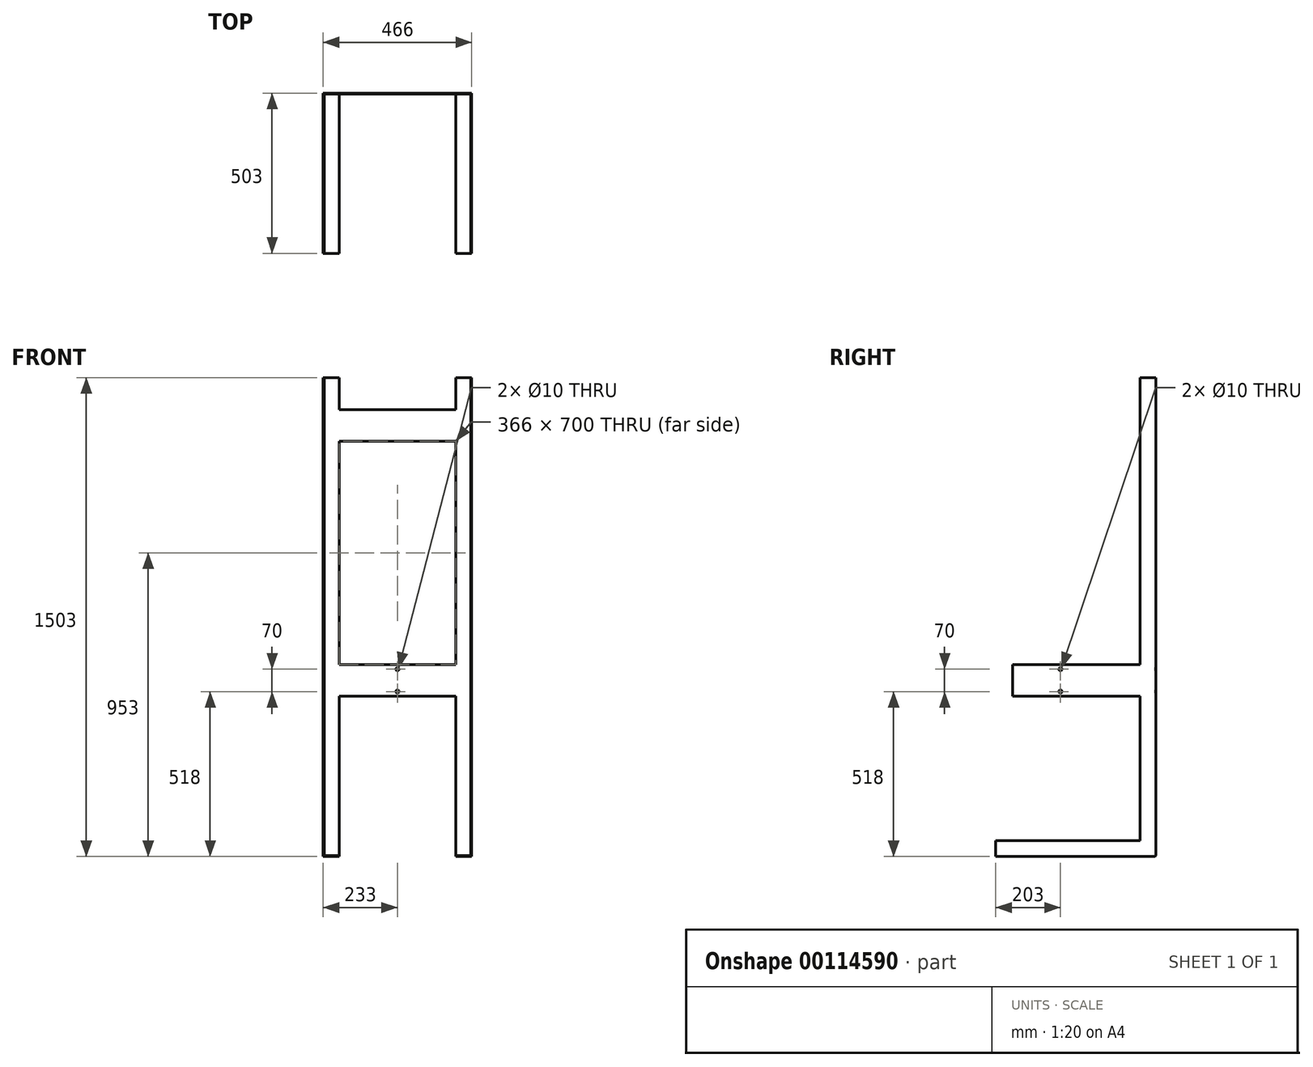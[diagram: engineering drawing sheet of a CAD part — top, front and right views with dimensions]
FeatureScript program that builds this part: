
annotation { "Feature Type Name" : "Feature", "Feature Type Description" : "" }
export const myFeature = defineFeature(function(context is Context, id is Id, definition is map)
    precondition{}
    {
        {
            var Q0;
            Q0=qCreatedBy(makeId("Top.planeOp"),FACE);
            var sketch = newSketch(context, id + "F0", { "sketchPlane" : qUnion([Q0])});
            skLineSegment(sketch, "E0", {"start": v(-233, 225) * mm, "end": v(-233, 175) * mm});
            skLineSegment(sketch, "E1", {"start": v(-233, 175) * mm, "end": v(-230, 175) * mm});
            skLineSegment(sketch, "E2", {"start": v(-230, 175) * mm, "end": v(-230, 222) * mm});
            skLineSegment(sketch, "E3", {"start": v(-183, 222) * mm, "end": v(-230, 222) * mm});
            skLineSegment(sketch, "E4", {"start": v(-233, 225) * mm, "end": v(-183, 225) * mm});
            skLineSegment(sketch, "E5", {"start": v(-183, 222) * mm, "end": v(-183, 225) * mm});
            skSolve(sketch);
        }
        {
            var Q0;
            Q0=makeQuery(id+"F0.imprint","IMPRINT",FACE,{"disambiguationData":[TD([[makeQuery(id+"F0.imprint","IMPRINT",EDGE,{"derivedFrom":sQuery(id+"F0.wireOp",EDGE,"E0")}),1.0]])]});
            extrude(context, id + "F1", {"entities" : qUnion([Q0]), "depth" : 1500 * mm});
        }
        {
            var Q0;
            Q0=makeQuery(id+"F1.opExtrude","SWEPT_FACE",FACE,{"disambiguationData":[OSD([sQuery(id+"F0.wireOp",EDGE,"E5")])]});
            var sketch = newSketch(context, id + "F2", { "sketchPlane" : qUnion([Q0])});
            skLineSegment(sketch, "E6", {"start": v(222, 0) * mm, "end": v(222, -3) * mm});
            skLineSegment(sketch, "E7", {"start": v(222, -3) * mm, "end": v(225, 0) * mm});
            skSolve(sketch);
        }
        {
            var Q0;
            {var subQ0=sQuery(id+"F2.wireOp",EDGE,"E6");Q0=makeQuery(id+"F2.imprint","IMPRINT",FACE,{"disambiguationData":[TD([[makeQuery(id+"F2.imprint","IMPRINT",EDGE,{"derivedFrom":subQ0}),1.0]])]});}
            extrude(context, id + "F3", {"entities" : qUnion([Q0]), "operationType" : NewBodyOperationType.ADD, "oppositeDirection" : true, "depth" : 50 * mm});
        }
        {
            var Q0;
            Q0=makeQuery(id+"F3.boolean.opBoolean","MERGE",FACE,{"derivedFrom":[makeQuery(id+"F1.opExtrude","SWEPT_FACE",FACE,{"disambiguationData":[OSD([sQuery(id+"F0.wireOp",EDGE,"E3")])]}),makeQuery(id+"F3.opExtrude","SWEPT_FACE",FACE,{"disambiguationData":[OSD([sQuery(id+"F2.wireOp",EDGE,"E6")])]})]});
            var sketch = newSketch(context, id + "F4", { "sketchPlane" : qUnion([Q0])});
            skLineSegment(sketch, "E8", {"start": v(-233, -3) * mm, "end": v(-183, -3) * mm});
            skLineSegment(sketch, "E9", {"start": v(-183, -3) * mm, "end": v(-183, 0) * mm});
            skLineSegment(sketch, "E10", {"start": v(-183, 0) * mm, "end": v(-230, 0) * mm});
            skLineSegment(sketch, "E11", {"start": v(-230, 47) * mm, "end": v(-230, 0) * mm});
            skLineSegment(sketch, "E12", {"start": v(-233, -3) * mm, "end": v(-233, 47) * mm});
            skLineSegment(sketch, "E13", {"start": v(-230, 47) * mm, "end": v(-233, 47) * mm});
            skSolve(sketch);
        }
        {
            var Q0;
            Q0 = qSketchRegion(id + "F4", true);
            extrude(context, id + "F5", {"entities" : qUnion([Q0]), "operationType" : NewBodyOperationType.ADD, "depth" : 500 * mm});
        }
        {
            var Q0;
            {var subQ0=sQuery(id+"F0.wireOp",EDGE,"E5");Q0=makeQuery(id+"F5.boolean.opBoolean","MERGE",FACE,{"derivedFrom":[makeQuery(id+"F3.boolean.opBoolean","MERGE",FACE,{"derivedFrom":[makeQuery(id+"F1.opExtrude","SWEPT_FACE",FACE,{"disambiguationData":[OSD([subQ0])]}),makeQuery(id+"F3.opExtrude","CAP_FACE",FACE,{"disambiguationData":[OSD([subQ0,sQuery(id+"F2.wireOp",EDGE,"E6"),sQuery(id+"F2.wireOp",EDGE,"E7")])],"isStart":true})]}),makeQuery(id+"F5.opExtrude","SWEPT_FACE",FACE,{"disambiguationData":[OSD([sQuery(id+"F4.wireOp",EDGE,"E9")])]})]});}
            var sketch = newSketch(context, id + "F6", { "sketchPlane" : qUnion([Q0])});
            skLineSegment(sketch, "E14.bottom", {"start": v(222, 1400) * mm, "end": v(225, 1400) * mm});
            skLineSegment(sketch, "E14.top", {"start": v(222, 1300) * mm, "end": v(225, 1300) * mm});
            skLineSegment(sketch, "E14.left", {"start": v(222, 1400) * mm, "end": v(222, 1300) * mm});
            skLineSegment(sketch, "E14.right", {"start": v(225, 1400) * mm, "end": v(225, 1300) * mm});
            skLineSegment(sketch, "E15.bottom", {"start": v(222, 500) * mm, "end": v(225, 500) * mm});
            skLineSegment(sketch, "E15.top", {"start": v(222, 600) * mm, "end": v(225, 600) * mm});
            skLineSegment(sketch, "E15.left", {"start": v(222, 500) * mm, "end": v(222, 600) * mm});
            skLineSegment(sketch, "E15.right", {"start": v(225, 500) * mm, "end": v(225, 600) * mm});
            skSolve(sketch);
        }
        {
            var Q0;
            Q0=makeQuery(id+"F5.boolean.opBoolean","MERGE",FACE,{"derivedFrom":[makeQuery(id+"F1.opExtrude","SWEPT_FACE",FACE,{"disambiguationData":[OSD([sQuery(id+"F0.wireOp",EDGE,"E2")])]}),makeQuery(id+"F5.opExtrude","SWEPT_FACE",FACE,{"disambiguationData":[OSD([sQuery(id+"F4.wireOp",EDGE,"E11")])]})]});
            cPlane(context, id + "F7", {"entities" : qUnion([Q0]), "cplaneType" : CPlaneType.OFFSET, "offset" : 230 * mm, "width" : 150 * mm, "height" : 150 * mm});
        }
        {
            var Q0;
            Q0=makeQuery(id+"F1.opExtrude","SWEPT_BODY",BODY,{"disambiguationData":[OSD([sQuery(id+"F0.wireOp",EDGE,"E0"),sQuery(id+"F0.wireOp",EDGE,"E1"),sQuery(id+"F0.wireOp",EDGE,"E2"),sQuery(id+"F0.wireOp",EDGE,"E3"),sQuery(id+"F0.wireOp",EDGE,"E4"),sQuery(id+"F0.wireOp",EDGE,"E5")])]});
            var Q1;
            Q1=qCreatedBy(id+"F7.planeOp",FACE);
            mirror(context, id + "F8", {"entities" : qUnion([Q0]), "mirrorPlane" : qUnion([Q1])});
        }
        {
            var Q0;
            Q0 = qSketchRegion(id + "F6", true);
            var Q1;
            {var subQ0=sQuery(id+"F0.wireOp",EDGE,"E5");Q1=makeQuery(id+"F8.opPattern","COPY",FACE,{"derivedFrom":makeQuery(id+"F5.boolean.opBoolean","MERGE",FACE,{"derivedFrom":[makeQuery(id+"F3.boolean.opBoolean","MERGE",FACE,{"derivedFrom":[makeQuery(id+"F1.opExtrude","SWEPT_FACE",FACE,{"disambiguationData":[OSD([subQ0])]}),makeQuery(id+"F3.opExtrude","CAP_FACE",FACE,{"disambiguationData":[OSD([subQ0,sQuery(id+"F2.wireOp",EDGE,"E6"),sQuery(id+"F2.wireOp",EDGE,"E7")])],"isStart":true})]}),makeQuery(id+"F5.opExtrude","SWEPT_FACE",FACE,{"disambiguationData":[OSD([sQuery(id+"F4.wireOp",EDGE,"E9")])]})]}),"instanceName":"1"});}
            extrude(context, id + "F9", {"entities" : qUnion([Q0]), "operationType" : NewBodyOperationType.ADD, "endBound" : BoundingType.UP_TO_SURFACE, "endBoundEntityFace" : qUnion([Q1]), "depth" : 25 * mm});
        }
        {
            var Q0;
            {var subQ0=makeQuery(id+"F3.boolean.opBoolean","MERGE",FACE,{"derivedFrom":[makeQuery(id+"F1.opExtrude","SWEPT_FACE",FACE,{"disambiguationData":[OSD([sQuery(id+"F0.wireOp",EDGE,"E3")])]}),makeQuery(id+"F3.opExtrude","SWEPT_FACE",FACE,{"disambiguationData":[OSD([sQuery(id+"F2.wireOp",EDGE,"E6")])]})]});Q0=makeQuery(id+"F9.boolean.opBoolean","MERGE",FACE,{"derivedFrom":[subQ0,makeQuery(id+"F8.opPattern","COPY",FACE,{"derivedFrom":subQ0,"instanceName":"1"}),makeQuery(id+"F9.opExtrude","SWEPT_FACE",FACE,{"disambiguationData":[OSD([sQuery(id+"F6.wireOp",EDGE,"E14.left")])]}),makeQuery(id+"F9.opExtrude","SWEPT_FACE",FACE,{"disambiguationData":[OSD([sQuery(id+"F6.wireOp",EDGE,"E15.left")])]})]});}
            var sketch = newSketch(context, id + "F10", { "sketchPlane" : qUnion([Q0])});
            skCircle(sketch, "E16", {"center": v(0, 585) * mm, "radius": 5 * mm});
            skLineSegment(sketch, "E17", {"start": v(0, 600) * mm, "end": v(0, 500) * mm, "construction": true});
            skCircle(sketch, "E18", {"center": v(0, 515) * mm, "radius": 5 * mm});
            skSolve(sketch);
        }
        {
            var Q0;
            Q0=makeQuery(id+"F10.imprint","IMPRINT",FACE,{"disambiguationData":[TD([[makeQuery(id+"F10.imprint","IMPRINT",EDGE,{"derivedFrom":sQuery(id+"F10.wireOp",EDGE,"E16")}),1.0]])]});
            var Q1;
            Q1=makeQuery(id+"F10.imprint","IMPRINT",FACE,{"disambiguationData":[TD([[makeQuery(id+"F10.imprint","IMPRINT",EDGE,{"derivedFrom":sQuery(id+"F10.wireOp",EDGE,"E18")}),1.0]])]});
            extrude(context, id + "F11", {"entities" : qUnion([Q0, Q1]), "operationType" : NewBodyOperationType.REMOVE, "oppositeDirection" : true, "depth" : 25 * mm, "offsetDistance" : 25 * mm});
        }
        {
            var Q0;
            Q0=makeQuery(id+"F8.opPattern","COPY",FACE,{"derivedFrom":makeQuery(id+"F1.opExtrude","SWEPT_FACE",FACE,{"disambiguationData":[OSD([sQuery(id+"F0.wireOp",EDGE,"E1")])]}),"instanceName":"1"});
            var sketch = newSketch(context, id + "F12", { "sketchPlane" : qUnion([Q0])});
            skLineSegment(sketch, "E19.bottom", {"start": v(230, 600) * mm, "end": v(233, 600) * mm});
            skLineSegment(sketch, "E19.top", {"start": v(230, 500) * mm, "end": v(233, 500) * mm});
            skLineSegment(sketch, "E19.left", {"start": v(230, 600) * mm, "end": v(230, 500) * mm});
            skLineSegment(sketch, "E19.right", {"start": v(233, 600) * mm, "end": v(233, 500) * mm});
            skSolve(sketch);
        }
        {
            var Q0;
            Q0=makeQuery(id+"F12.imprint","IMPRINT",FACE,{"disambiguationData":[TD([[makeQuery(id+"F12.imprint","IMPRINT",EDGE,{"derivedFrom":sQuery(id+"F12.wireOp",EDGE,"E19.bottom")}),-1.0]])]});
            extrude(context, id + "F13", {"entities" : qUnion([Q0]), "operationType" : NewBodyOperationType.ADD, "depth" : 400 * mm, "offsetDistance" : 25 * mm});
        }
        {
            var Q0;
            Q0=makeQuery(id+"F13.boolean.opBoolean","MERGE",FACE,{"derivedFrom":[makeQuery(id+"F8.opPattern","COPY",FACE,{"derivedFrom":makeQuery(id+"F5.boolean.opBoolean","MERGE",FACE,{"derivedFrom":[makeQuery(id+"F3.boolean.opBoolean","MERGE",FACE,{"derivedFrom":[makeQuery(id+"F1.opExtrude","SWEPT_FACE",FACE,{"disambiguationData":[OSD([sQuery(id+"F0.wireOp",EDGE,"E0")])]}),makeQuery(id+"F3.opExtrude","CAP_FACE",FACE,{"disambiguationData":[OSD([sQuery(id+"F0.wireOp",EDGE,"E5"),sQuery(id+"F2.wireOp",EDGE,"E6"),sQuery(id+"F2.wireOp",EDGE,"E7")])],"isStart":false})]}),makeQuery(id+"F5.opExtrude","SWEPT_FACE",FACE,{"disambiguationData":[OSD([sQuery(id+"F4.wireOp",EDGE,"E12")])]})]}),"instanceName":"1"}),makeQuery(id+"F13.opExtrude","SWEPT_FACE",FACE,{"disambiguationData":[OSD([sQuery(id+"F12.wireOp",EDGE,"E19.right")])]})]});
            var sketch = newSketch(context, id + "F14", { "sketchPlane" : qUnion([Q0])});
            skLineSegment(sketch, "E20", {"start": v(-75, 600) * mm, "end": v(-75, 500) * mm, "construction": true});
            skCircle(sketch, "E21", {"center": v(-75, 585) * mm, "radius": 5 * mm});
            skCircle(sketch, "E22", {"center": v(-75, 515) * mm, "radius": 5 * mm});
            skSolve(sketch);
        }
        {
            var Q0;
            Q0=makeQuery(id+"F14.imprint","IMPRINT",FACE,{"disambiguationData":[TD([[makeQuery(id+"F14.imprint","IMPRINT",EDGE,{"derivedFrom":sQuery(id+"F14.wireOp",EDGE,"E21")}),1.0]])]});
            var Q1;
            Q1=makeQuery(id+"F14.imprint","IMPRINT",FACE,{"disambiguationData":[TD([[makeQuery(id+"F14.imprint","IMPRINT",EDGE,{"derivedFrom":sQuery(id+"F14.wireOp",EDGE,"E22")}),1.0]])]});
            extrude(context, id + "F15", {"entities" : qUnion([Q0, Q1]), "operationType" : NewBodyOperationType.REMOVE, "oppositeDirection" : true, "depth" : 25 * mm, "offsetDistance" : 25 * mm});
        }
    });
